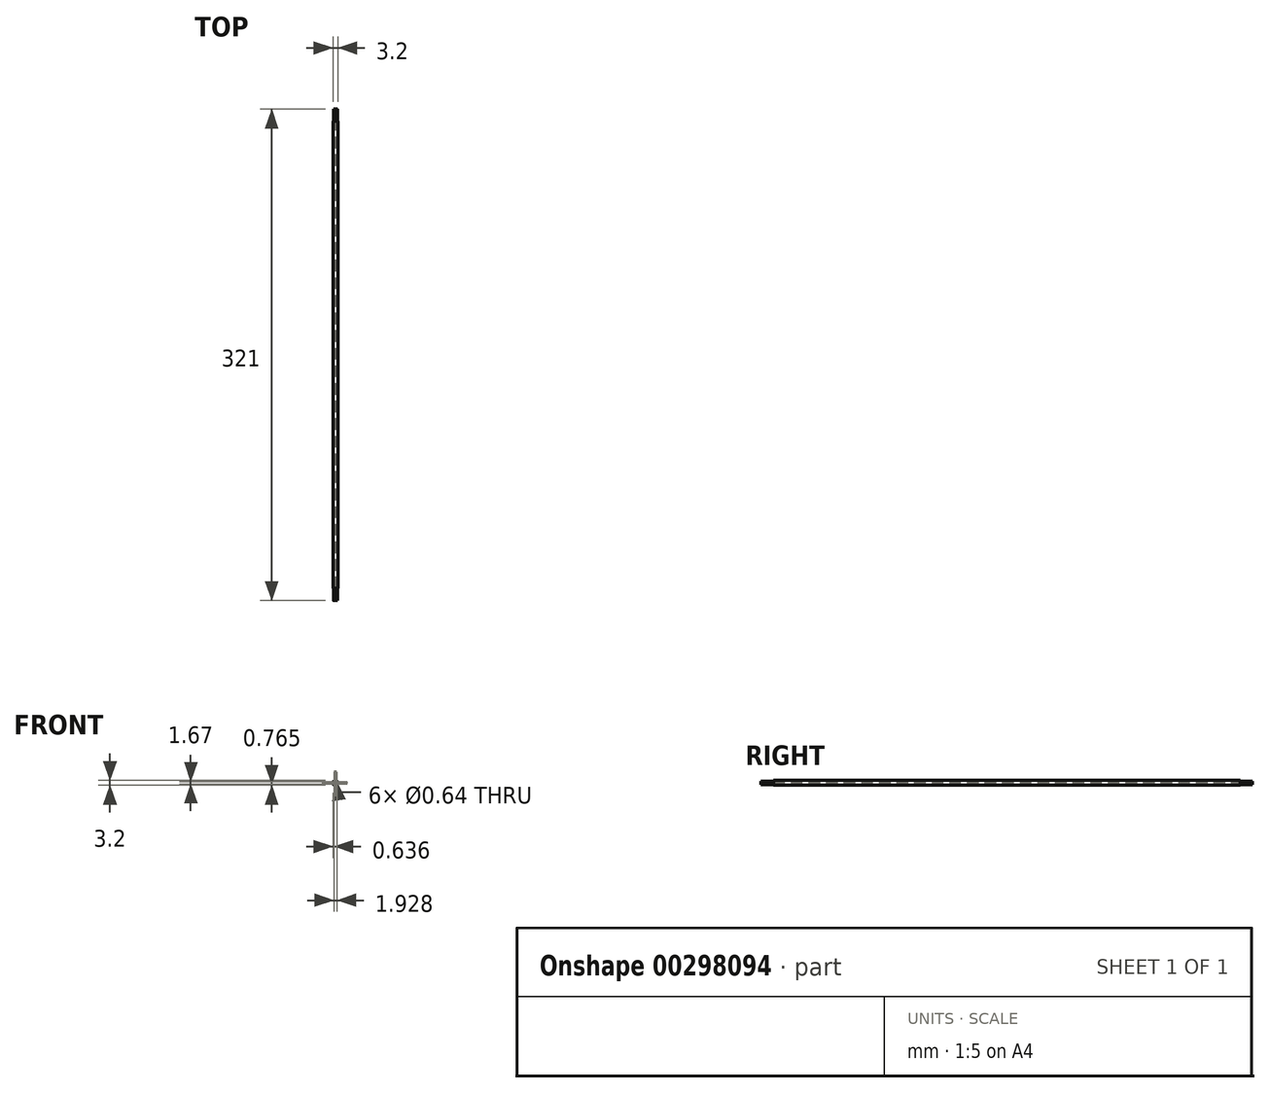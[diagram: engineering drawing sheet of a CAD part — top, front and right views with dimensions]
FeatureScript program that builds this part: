
annotation { "Feature Type Name" : "Feature", "Feature Type Description" : "" }
export const myFeature = defineFeature(function(context is Context, id is Id, definition is map)
    precondition{}
    {
        {
            var Q0;
            Q0=qCreatedBy(makeId("Front.planeOp"),FACE);
            var sketch = newSketch(context, id + "F0", { "sketchPlane" : qUnion([Q0])});
            skCircle(sketch, "E0", {"center": v(0.96, 0) * mm, "radius": 0.32 * mm});
            skCircle(sketch, "E1.1.0", {"center": v(0.48, 0.83) * mm, "radius": 0.32 * mm});
            skCircle(sketch, "E1.2.0", {"center": v(-0.48, 0.83) * mm, "radius": 0.32 * mm});
            skCircle(sketch, "E1.3.0", {"center": v(-0.96, 0) * mm, "radius": 0.32 * mm});
            skCircle(sketch, "E1.4.0", {"center": v(-0.48, -0.83) * mm, "radius": 0.32 * mm});
            skPoint(sketch, "E1.center", {"position": v(0, 0) * mm});
            skCircle(sketch, "E2", {"center": v(0, 0) * mm, "radius": 1.6 * mm});
            skCircle(sketch, "E3.1.5.0", {"center": v(0.48, -0.83) * mm, "radius": 0.32 * mm});
            skSolve(sketch);
        }
        {
            var Q0;
            Q0=makeQuery(id+"F0.imprint","IMPRINT",FACE,{"disambiguationData":[TD([[makeQuery(id+"F0.imprint","IMPRINT",EDGE,{"derivedFrom":sQuery(id+"F0.wireOp",EDGE,"E0")}),-1.0]])]});
            extrude(context, id + "F1", {"entities" : qUnion([Q0]), "depth" : 305 * mm});
        }
        {
            var Q0;
            Q0=makeQuery(id+"F1.opExtrude","CAP_FACE",FACE,{"disambiguationData":[OSD([sQuery(id+"F0.wireOp",EDGE,"E0"),sQuery(id+"F0.wireOp",EDGE,"E1.1.0"),sQuery(id+"F0.wireOp",EDGE,"E1.2.0"),sQuery(id+"F0.wireOp",EDGE,"E1.3.0"),sQuery(id+"F0.wireOp",EDGE,"E1.4.0"),sQuery(id+"F0.wireOp",EDGE,"E2"),sQuery(id+"F0.wireOp",EDGE,"E3.1.5.0")])],"isStart":false});
            var sketch = newSketch(context, id + "F2", { "sketchPlane" : qUnion([Q0])});
            skCircle(sketch, "E4.0.0", {"center": v(0, 0) * mm, "radius": 1.6 * mm});
            skSolve(sketch);
        }
        {
            var Q0;
            Q0=makeQuery(id+"F2.imprint","IMPRINT",FACE,{"disambiguationData":[TD([[makeQuery(id+"F2.imprint","IMPRINT",EDGE,{"derivedFrom":makeQuery(id+"F1.opExtrude","CAP_EDGE",EDGE,{"disambiguationData":[OSD([sQuery(id+"F0.wireOp",EDGE,"E1.2.0")])],"isStart":false})}),1.0]])]});
            var Q1;
            Q1=makeQuery(id+"F2.imprint","IMPRINT",FACE,{"disambiguationData":[TD([[makeQuery(id+"F2.imprint","IMPRINT",EDGE,{"derivedFrom":makeQuery(id+"F1.opExtrude","CAP_EDGE",EDGE,{"disambiguationData":[OSD([sQuery(id+"F0.wireOp",EDGE,"E1.1.0")])],"isStart":false})}),1.0]])]});
            var Q2;
            Q2=makeQuery(id+"F2.imprint","IMPRINT",FACE,{"disambiguationData":[TD([[makeQuery(id+"F2.imprint","IMPRINT",EDGE,{"derivedFrom":makeQuery(id+"F1.opExtrude","CAP_EDGE",EDGE,{"disambiguationData":[OSD([sQuery(id+"F0.wireOp",EDGE,"E1.3.0")])],"isStart":false})}),1.0]])]});
            var Q3;
            Q3=makeQuery(id+"F2.imprint","IMPRINT",FACE,{"disambiguationData":[TD([[makeQuery(id+"F2.imprint","IMPRINT",EDGE,{"derivedFrom":makeQuery(id+"F1.opExtrude","CAP_EDGE",EDGE,{"disambiguationData":[OSD([sQuery(id+"F0.wireOp",EDGE,"E1.4.0")])],"isStart":false})}),1.0]])]});
            var Q4;
            Q4=makeQuery(id+"F2.imprint","IMPRINT",FACE,{"disambiguationData":[TD([[makeQuery(id+"F2.imprint","IMPRINT",EDGE,{"derivedFrom":makeQuery(id+"F1.opExtrude","CAP_EDGE",EDGE,{"disambiguationData":[OSD([sQuery(id+"F0.wireOp",EDGE,"E3.1.5.0")])],"isStart":false})}),1.0]])]});
            var Q5;
            Q5=makeQuery(id+"F2.imprint","IMPRINT",FACE,{"disambiguationData":[TD([[makeQuery(id+"F2.imprint","IMPRINT",EDGE,{"derivedFrom":makeQuery(id+"F1.opExtrude","CAP_EDGE",EDGE,{"disambiguationData":[OSD([sQuery(id+"F0.wireOp",EDGE,"E0")])],"isStart":false})}),1.0]])]});
            extrude(context, id + "F3", {"entities" : qUnion([Q0, Q1, Q2, Q3, Q4, Q5]), "depth" : 8 * mm});
        }
        {
            var Q0;
            Q0=makeQuery(id+"F1.opExtrude","CAP_FACE",FACE,{"disambiguationData":[OSD([sQuery(id+"F0.wireOp",EDGE,"E0"),sQuery(id+"F0.wireOp",EDGE,"E1.1.0"),sQuery(id+"F0.wireOp",EDGE,"E1.2.0"),sQuery(id+"F0.wireOp",EDGE,"E1.3.0"),sQuery(id+"F0.wireOp",EDGE,"E1.4.0"),sQuery(id+"F0.wireOp",EDGE,"E2"),sQuery(id+"F0.wireOp",EDGE,"E3.1.5.0")])],"isStart":true});
            var sketch = newSketch(context, id + "F4", { "sketchPlane" : qUnion([Q0])});
            skCircle(sketch, "E5.0.0", {"center": v(0, 0) * mm, "radius": 1.6 * mm});
            skSolve(sketch);
        }
        {
            var Q0;
            Q0=makeQuery(id+"F4.imprint","IMPRINT",FACE,{"disambiguationData":[TD([[makeQuery(id+"F4.imprint","IMPRINT",EDGE,{"derivedFrom":makeQuery(id+"F1.opExtrude","CAP_EDGE",EDGE,{"disambiguationData":[OSD([sQuery(id+"F0.wireOp",EDGE,"E1.1.0")])],"isStart":true})}),-1.0]])]});
            var Q1;
            Q1=makeQuery(id+"F4.imprint","IMPRINT",FACE,{"disambiguationData":[TD([[makeQuery(id+"F4.imprint","IMPRINT",EDGE,{"derivedFrom":makeQuery(id+"F1.opExtrude","CAP_EDGE",EDGE,{"disambiguationData":[OSD([sQuery(id+"F0.wireOp",EDGE,"E0")])],"isStart":true})}),-1.0]])]});
            var Q2;
            Q2=makeQuery(id+"F4.imprint","IMPRINT",FACE,{"disambiguationData":[TD([[makeQuery(id+"F4.imprint","IMPRINT",EDGE,{"derivedFrom":makeQuery(id+"F1.opExtrude","CAP_EDGE",EDGE,{"disambiguationData":[OSD([sQuery(id+"F0.wireOp",EDGE,"E3.1.5.0")])],"isStart":true})}),-1.0]])]});
            var Q3;
            Q3=makeQuery(id+"F4.imprint","IMPRINT",FACE,{"disambiguationData":[TD([[makeQuery(id+"F4.imprint","IMPRINT",EDGE,{"derivedFrom":makeQuery(id+"F1.opExtrude","CAP_EDGE",EDGE,{"disambiguationData":[OSD([sQuery(id+"F0.wireOp",EDGE,"E1.2.0")])],"isStart":true})}),-1.0]])]});
            var Q4;
            Q4=makeQuery(id+"F4.imprint","IMPRINT",FACE,{"disambiguationData":[TD([[makeQuery(id+"F4.imprint","IMPRINT",EDGE,{"derivedFrom":makeQuery(id+"F1.opExtrude","CAP_EDGE",EDGE,{"disambiguationData":[OSD([sQuery(id+"F0.wireOp",EDGE,"E1.3.0")])],"isStart":true})}),-1.0]])]});
            var Q5;
            Q5=makeQuery(id+"F4.imprint","IMPRINT",FACE,{"disambiguationData":[TD([[makeQuery(id+"F4.imprint","IMPRINT",EDGE,{"derivedFrom":makeQuery(id+"F1.opExtrude","CAP_EDGE",EDGE,{"disambiguationData":[OSD([sQuery(id+"F0.wireOp",EDGE,"E1.4.0")])],"isStart":true})}),-1.0]])]});
            extrude(context, id + "F5", {"entities" : qUnion([Q0, Q1, Q2, Q3, Q4, Q5]), "depth" : 8 * mm});
        }
    });
